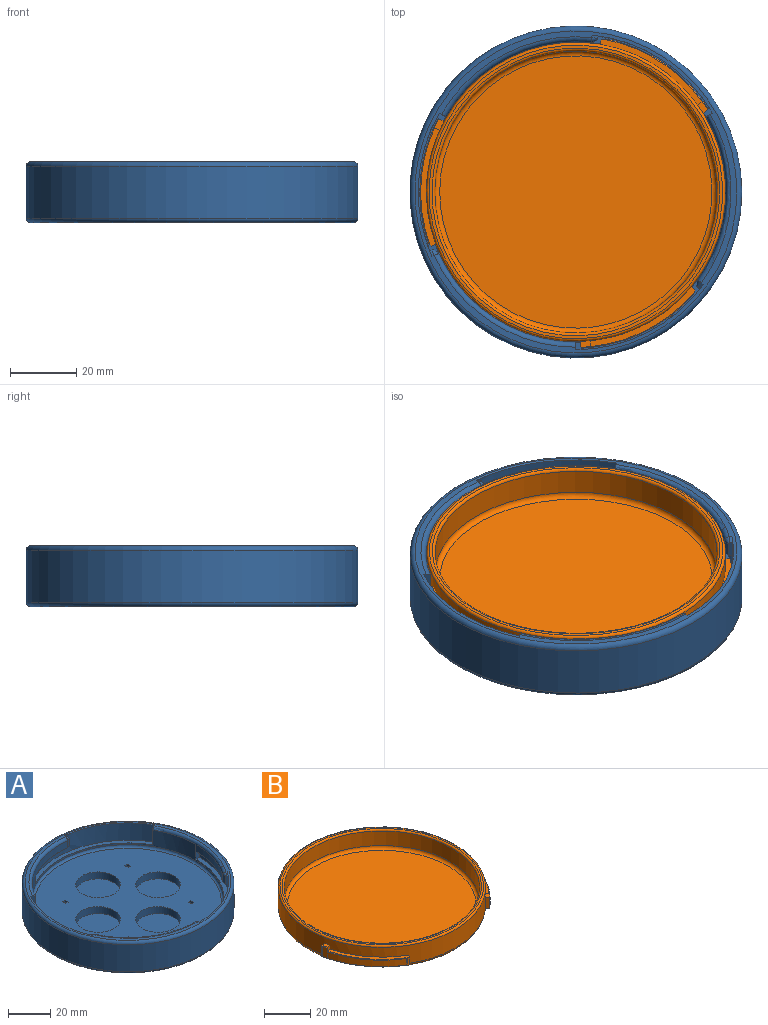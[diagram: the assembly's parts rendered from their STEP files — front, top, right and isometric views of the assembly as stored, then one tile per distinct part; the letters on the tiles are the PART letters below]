
ASSEMBLY  parts=2 mates=1
PART A: 73 faces, bbox 108.3x108.3x18.3 mm
  f0: plane 88x88mm, normal (0,0,1), area 4683.2mm2, adj f24,f30,f31,f32,f33,f35,f36,f37
  f1: plane 4.82x1.21mm, normal (-0.37,0.93,0), area 6.1mm2, adj f4,f5,f61,f62,f63,f68
  f2: plane 10x1.95mm, normal (-0.5,-0.87,0), area 22mm2, adj f5,f6,f13,f14,f26
  f3: plane 4.45x1.95mm, normal (-0.87,0.5,0), area 9.5mm2, adj f4,f5,f6,f14,f67
  f4: plane 23.71x21.29mm, normal (0,0,-1), area 60.8mm2, adj f1,f3,f5,f67,f68
  f5: cylinder r=47.5mm len=64.89mm, axis (0,0,-1), area 564.3mm2, adj f1,f2,f3,f4,f6,f13,f63
  f6: plane 64.89x24.88mm, normal (0,0,1), area 163.9mm2, adj f2,f3,f5,f14
  f7: plane 4.82x1.29mm, normal (0.99,-0.14,0), area 6.1mm2, adj f10,f11,f58,f59,f60,f72
  f8: plane 10x1.95mm, normal (-0.5,0.87,0), area 22mm2, adj f11,f12,f13,f14,f27
  f9: plane 4.45x1.95mm, normal (0.87,0.5,0), area 9.5mm2, adj f10,f11,f12,f14,f71
  f10: plane 30.36x8.1mm, normal (0,0,-1), area 60.8mm2, adj f7,f9,f11,f71,f72
  f11: cylinder r=47.5mm len=64.89mm, axis (0,0,-1), area 564.3mm2, adj f7,f8,f9,f10,f12,f13,f60
  f12: plane 64.89x24.88mm, normal (0,0,1), area 163.9mm2, adj f8,f9,f11,f14
  f13: plane 97x97mm, normal (0,0,1), area 423.6mm2, adj f2,f5,f8,f11,f19,f21,f26,f27
  f14: cylinder r=45.25mm len=90.5mm, axis (0,0,-1), area 1103.6mm2, adj f2,f3,f6,f8,f9,f12,f15,f18
  f15: cylinder r=45.25mm len=26.5mm, axis (0,0,-1), area 114.7mm2, adj f14,f27,f64,f69
  f16: cylinder r=50mm len=100mm, axis (0,0,-1), area 4885.2mm2, adj f25,f29
  f17: plane 97.5x97.5mm, normal (0,0,-1), area 7466.2mm2, adj f25
  f18: plane 4.45x2.25mm, normal (0,-1,0), area 9.5mm2, adj f14,f20,f21,f22,f69
  f19: plane 10x2.25mm, normal (1,0,0), area 22mm2, adj f13,f14,f20,f21,f28
  f20: plane 47.5x47.5mm, normal (0,0,1), area 163.9mm2, adj f14,f18,f19,f21
  f21: cylinder r=47.5mm len=47.5mm, axis (0,0,-1), area 564.3mm2, adj f13,f18,f19,f20,f22,f23,f66
  f22: plane 29.24x10.85mm, normal (0,0,-1), area 60.8mm2, adj f18,f21,f23,f69,f70
  f23: plane 4.82x1.03mm, normal (-0.62,-0.79,0), area 6.1mm2, adj f21,f22,f64,f65,f66,f70
  f24: torus R=44mm, axis (0,0,1), area 552.6mm2, adj f0,f14
  f25: torus R=48.75mm, axis (0,0,1), area 611.2mm2, adj f16,f17
  f26: torus R=46.75mm, axis (0,0,1), area 124mm2, adj f2,f13,f14,f59
  f27: torus R=46.75mm, axis (0,0,1), area 124mm2, adj f8,f13,f14,f15,f65
  f28: torus R=46.75mm, axis (0,0,1), area 124mm2, adj f13,f14,f19,f62
  f29: torus R=48.5mm, axis (0,0,1), area 732.2mm2, adj f13,f16
  f30: plane 1.6x1mm, normal (0,-1,0), area 1.6mm2, adj f0,f31,f33,f34
  f31: plane 2.1x1mm, normal (1,0,0), area 2.1mm2, adj f0,f30,f32,f34
  f32: plane 1.6x1mm, normal (0,1,0), area 1.6mm2, adj f0,f31,f33,f34
  f33: plane 2.1x1mm, normal (-1,0,0), area 2.1mm2, adj f0,f30,f32,f34
  f34: plane 2.1x1.6mm, normal (0,0,1), area 3.4mm2, adj f30,f31,f32,f33
  f35: plane 2.1x1mm, normal (-1,0,0), area 2.1mm2, adj f0,f36,f38,f39
  f36: plane 1.6x1mm, normal (0,-1,0), area 1.6mm2, adj f0,f35,f37,f39
  f37: plane 2.1x1mm, normal (1,0,0), area 2.1mm2, adj f0,f36,f38,f39
  f38: plane 1.6x1mm, normal (0,1,0), area 1.6mm2, adj f0,f35,f37,f39
  f39: plane 2.1x1.6mm, normal (0,0,1), area 3.4mm2, adj f35,f36,f37,f38
  f40: plane 1.6x1mm, normal (0,-1,0), area 1.6mm2, adj f0,f41,f43,f44
  f41: plane 2.1x1mm, normal (1,0,0), area 2.1mm2, adj f0,f40,f42,f44
  f42: plane 1.6x1mm, normal (0,1,0), area 1.6mm2, adj f0,f41,f43,f44
  f43: plane 2.1x1mm, normal (-1,0,0), area 2.1mm2, adj f0,f40,f42,f44
  f44: plane 2.1x1.6mm, normal (0,0,1), area 3.4mm2, adj f40,f41,f42,f43
  f45: plane 2.1x1mm, normal (1,0,0), area 2.1mm2, adj f0,f46,f48,f49
  f46: plane 1.6x1mm, normal (0,1,0), area 1.6mm2, adj f0,f45,f47,f49
  f47: plane 2.1x1mm, normal (-1,0,0), area 2.1mm2, adj f0,f46,f48,f49
  f48: plane 1.6x1mm, normal (0,-1,0), area 1.6mm2, adj f0,f45,f47,f49
  f49: plane 2.1x1.6mm, normal (0,0,1), area 3.4mm2, adj f45,f46,f47,f48
  f50: cylinder r=10.5mm len=21mm, axis (0,0,1), area 263.9mm2, adj f0,f51
  f51: plane 21x21mm, normal (0,0,1), area 346.4mm2, adj f50
  f52: cylinder r=10.5mm len=21mm, axis (0,0,1), area 263.9mm2, adj f0,f53
  f53: plane 21x21mm, normal (0,0,1), area 346.4mm2, adj f52
  f54: cylinder r=10.5mm len=21mm, axis (0,0,1), area 263.9mm2, adj f0,f55
  f55: plane 21x21mm, normal (0,0,1), area 346.4mm2, adj f54
  f56: cylinder r=10.5mm len=21mm, axis (0,0,1), area 263.9mm2, adj f0,f57
  f57: plane 21x21mm, normal (0,0,1), area 346.4mm2, adj f56
  f58: plane 4.05x1.82mm, normal (0.38,-0.92,0), area 8mm2, adj f7,f14,f59,f72
  f59: bspline ~1.89x1.52mm, area 3.1mm2, adj f7,f26,f58,f60
  f60: plane 1.82x1mm, normal (0.5,-0.07,0.87), area 1.5mm2, adj f7,f11,f13,f59
  f61: plane 4.05x1.56mm, normal (0.61,0.79,0), area 8mm2, adj f1,f14,f62,f68
  f62: bspline ~2.04x1.8mm, area 3.1mm2, adj f1,f28,f61,f63
  f63: plane 1.89x1.37mm, normal (-0.19,0.46,0.87), area 1.5mm2, adj f1,f5,f13,f62
  f64: plane 4.05x1.95mm, normal (-0.99,0.13,0), area 8mm2, adj f15,f23,f65,f70
  f65: bspline ~2.27x1.52mm, area 3.1mm2, adj f23,f27,f64,f66
  f66: plane 1.85x1.66mm, normal (-0.31,-0.39,0.87), area 1.5mm2, adj f13,f21,f23,f65
  f67: cone r=45.5mm half-angle=45deg, axis (0,0,-1), area 10mm2, adj f3,f4,f14,f68
  f68: plane 1.83x1.36mm, normal (0.43,0.56,-0.71), area 0.7mm2, adj f1,f4,f61,f67
  f69: cone r=45.5mm half-angle=45deg, axis (0,0,-1), area 10mm2, adj f15,f18,f22,f70
  f70: plane 2.13x0.5mm, normal (-0.7,0.09,-0.71), area 0.7mm2, adj f22,f23,f64,f69
  f71: cone r=45.5mm half-angle=45deg, axis (0,0,-1), area 10mm2, adj f9,f10,f14,f72
  f72: plane 1.9x1.04mm, normal (0.27,-0.65,-0.71), area 0.7mm2, adj f7,f10,f58,f71
PART B: 60 faces, bbox 97.4x97.4x12 mm
  f0: cylinder r=45mm len=90mm, axis (0,0,-1), area 2264.5mm2, adj f6,f8,f9,f10,f12,f13,f14,f15
  f1: cylinder r=42.5mm len=85mm, axis (0,0,-1), area 2056.2mm2, adj f5,f7
  f2: plane 88.4x88.4mm, normal (0,0,1), area 247.4mm2, adj f7,f8
  f3: plane 87x87mm, normal (0,0,-1), area 5944.7mm2, adj f6
  f4: plane 82x82mm, normal (0,0,1), area 5281mm2, adj f5
  f5: torus R=41mm, axis (0,0,1), area 621.1mm2, adj f1,f4
  f6: torus R=43.5mm, axis (0,0,1), area 658.1mm2, adj f0,f3
  f7: torus R=43.3mm, axis (0,0,1), area 337.9mm2, adj f1,f2
  f8: torus R=44.2mm, axis (0,0,1), area 353mm2, adj f0,f2
  f9: plane 4x1.43mm, normal (0,1,0), area 5.7mm2, adj f0,f10,f12,f34
  f10: plane 35.18x17.12mm, normal (0,0,-1), area 68.3mm2, adj f0,f9,f13,f34,f39,f41
  f11: cylinder r=47mm len=31.96mm, axis (0,0,-1), area 124.7mm2, adj f16,f41,f42,f43
  f12: plane 33.06x14.93mm, normal (0,0,1), area 62.9mm2, adj f0,f9,f14,f34,f42
  f13: plane 6x1.31mm, normal (-0.71,-0.71,0), area 11.1mm2, adj f0,f10,f15,f37
  f14: plane 2x1.24mm, normal (0.71,0.71,0), area 3.5mm2, adj f0,f12,f15,f38
  f15: plane 3.43x3.36mm, normal (0,0,1), area 5.4mm2, adj f0,f13,f14,f36
  f16: plane 5.5x1.94mm, normal (0.71,-0.71,0), area 14.6mm2, adj f11,f36,f37,f38,f39,f40
  f17: cylinder r=47mm len=27.89mm, axis (0,0,-1), area 124.7mm2, adj f18,f49,f50,f51
  f18: plane 5.5x2.66mm, normal (-0.97,-0.26,0), area 14.6mm2, adj f17,f44,f45,f46,f47,f48
  f19: plane 3.38x2.47mm, normal (0,0,1), area 5.4mm2, adj f0,f20,f21,f44
  f20: plane 2x1.69mm, normal (0.26,-0.97,0), area 3.5mm2, adj f0,f19,f22,f46
  f21: plane 6x1.79mm, normal (-0.26,0.97,0), area 11.1mm2, adj f0,f19,f23,f45
  f22: plane 28.56x22.66mm, normal (0,0,1), area 62.9mm2, adj f0,f20,f24,f35,f50
  f23: plane 31.48x23.43mm, normal (0,0,-1), area 68.3mm2, adj f0,f21,f24,f35,f47,f49
  f24: plane 4x1.23mm, normal (0.87,-0.5,0), area 5.7mm2, adj f0,f22,f23,f35
  f25: plane 4x1.23mm, normal (-0.87,-0.5,0), area 5.7mm2, adj f0,f26,f28,f33
  f26: plane 38.21x7.78mm, normal (0,0,-1), area 68.3mm2, adj f0,f25,f29,f33,f52,f53
  f27: cylinder r=47mm len=34.55mm, axis (0,0,-1), area 124.7mm2, adj f32,f52,f54,f56
  f28: plane 35.31x7.78mm, normal (0,0,1), area 62.9mm2, adj f0,f25,f30,f33,f56
  f29: plane 6x1.79mm, normal (0.97,-0.26,0), area 11.1mm2, adj f0,f26,f31,f55
  f30: plane 2x1.69mm, normal (-0.97,0.26,0), area 3.5mm2, adj f0,f28,f31,f59
  f31: plane 3.35x2.56mm, normal (0,0,1), area 5.4mm2, adj f0,f29,f30,f57
  f32: plane 5.5x2.66mm, normal (0.26,0.97,0), area 14.6mm2, adj f27,f53,f55,f57,f58,f59
  f33: plane 4x1.05mm, normal (-0.82,0.58,0), area 5mm2, adj f25,f26,f28,f52,f54,f56
  f34: plane 4x1.16mm, normal (0.91,0.42,0), area 5mm2, adj f9,f10,f12,f41,f42,f43
  f35: plane 4x1.28mm, normal (-0.09,-1,0), area 5mm2, adj f22,f23,f24,f49,f50,f51
  f36: plane 2.12x2.12mm, normal (0.5,-0.5,0.71), area 1mm2, adj f15,f16,f37,f38
  f37: plane 6x0.35mm, normal (0,-1,0), area 2mm2, adj f13,f16,f36,f39
  f38: plane 2.25x0.35mm, normal (1,0,0), area 0.7mm2, adj f14,f16,f36,f40
  f39: plane 2.3x2.12mm, normal (0.5,-0.5,-0.71), area 1mm2, adj f10,f16,f37,f41
  f40: plane 0.35x0.25mm, normal (0.5,-0.5,0.71), area 0mm2, adj f16,f38,f42
  f41: cone r=46.75mm half-angle=45deg, axis (0,0,1), area 12.7mm2, adj f10,f11,f34,f39,f43
  f42: cone r=47mm half-angle=45deg, axis (0,0,-1), area 12.7mm2, adj f11,f12,f34,f40,f43
  f43: plane 3.55x0.11mm, normal (0.98,0.2,0), area 0.4mm2, adj f11,f34,f41,f42
  f44: plane 2.9x0.95mm, normal (-0.68,-0.18,0.71), area 1mm2, adj f18,f19,f45,f46
  f45: plane 6x0.31mm, normal (-0.87,0.5,0), area 2mm2, adj f18,f21,f44,f47
  f46: plane 2.25x0.31mm, normal (-0.5,-0.87,0), area 0.7mm2, adj f18,f20,f44,f48
  f47: plane 2.96x0.95mm, normal (-0.68,-0.18,-0.71), area 1mm2, adj f18,f23,f45,f49
  f48: plane 0.31x0.25mm, normal (-0.68,-0.18,0.71), area 0mm2, adj f18,f46,f50
  f49: cone r=46.75mm half-angle=45deg, axis (0,0,1), area 12.7mm2, adj f17,f23,f35,f47,f51
  f50: cone r=47mm half-angle=45deg, axis (0,0,-1), area 12.7mm2, adj f17,f22,f35,f48,f51
  f51: plane 3.55x0.11mm, normal (-0.32,-0.95,0), area 0.4mm2, adj f17,f35,f49,f50
  f52: cone r=46.75mm half-angle=45deg, axis (0,0,1), area 12.7mm2, adj f26,f27,f33,f53,f54
  f53: plane 2.9x1.02mm, normal (0.18,0.68,-0.71), area 1mm2, adj f26,f32,f52,f55
  f54: plane 3.55x0.09mm, normal (-0.66,0.75,0), area 0.4mm2, adj f27,f33,f52,f56
  f55: plane 6x0.31mm, normal (0.87,0.5,0), area 2mm2, adj f29,f32,f53,f57
  f56: cone r=47mm half-angle=45deg, axis (0,0,-1), area 12.7mm2, adj f27,f28,f33,f54,f58
  f57: plane 2.9x0.95mm, normal (0.18,0.68,0.71), area 1mm2, adj f31,f32,f55,f59
  f58: plane 0.31x0.25mm, normal (0.18,0.68,0.71), area 0mm2, adj f32,f56,f59
  f59: plane 2.25x0.31mm, normal (-0.5,0.87,0), area 0.7mm2, adj f30,f32,f57,f58
PLACE A at identity fixed
PLACE B rot(axis=(0,0,1),80.6deg) t=(0,0,0.1)mm
MATE revolute A.f14 <-> B.f0  axis (0,0,1) through (0,0,-2.2)mm
